# Revit family: FU_Stool_Sandler_Palm Beach 4-2
name_source: partatom
category: Furniture
units: mm (PartAtom-declared; Revit-internal decimal feet)

## family parameters
Always vertical = Yes
Cut with Voids When Loaded = No
OmniClass Number = 23.40.20.00
OmniClass Title = General Furniture and Specialties
Room Calculation Point = No
Shared = No
Work Plane-Based = No

## types (1)
- Palm Beach 4.2
    Default Elevation = 0 mm  [stored 0 ft]
    Depth = 530 mm  [stored 1.73885 ft]
    Description = Counter stool with solid beech frame with upholstered back with square button pattern. With kickplates. Produced to custom height per customer specification, from 23.5″-29″ seat height.
    Frame = Wood - Beech - Natural Oak
    Height = 1115 mm  [stored 3.65814 ft]
    Manufacturer = Sandler
    Model = Palm Beach 4.2
    Seat = Fabric - Gravity - Sunni CPC20
    URL = https://www.sandlerseating.com
    Width = 430 mm  [stored 1.41076 ft]

note: [stored X ft] marks values corroborated as IEEE doubles in the binary element streams (Revit-internal decimal feet)

## geometry (parser evidence)
native form markers: Sweep x8
no freeform markers — native parametric forms only
